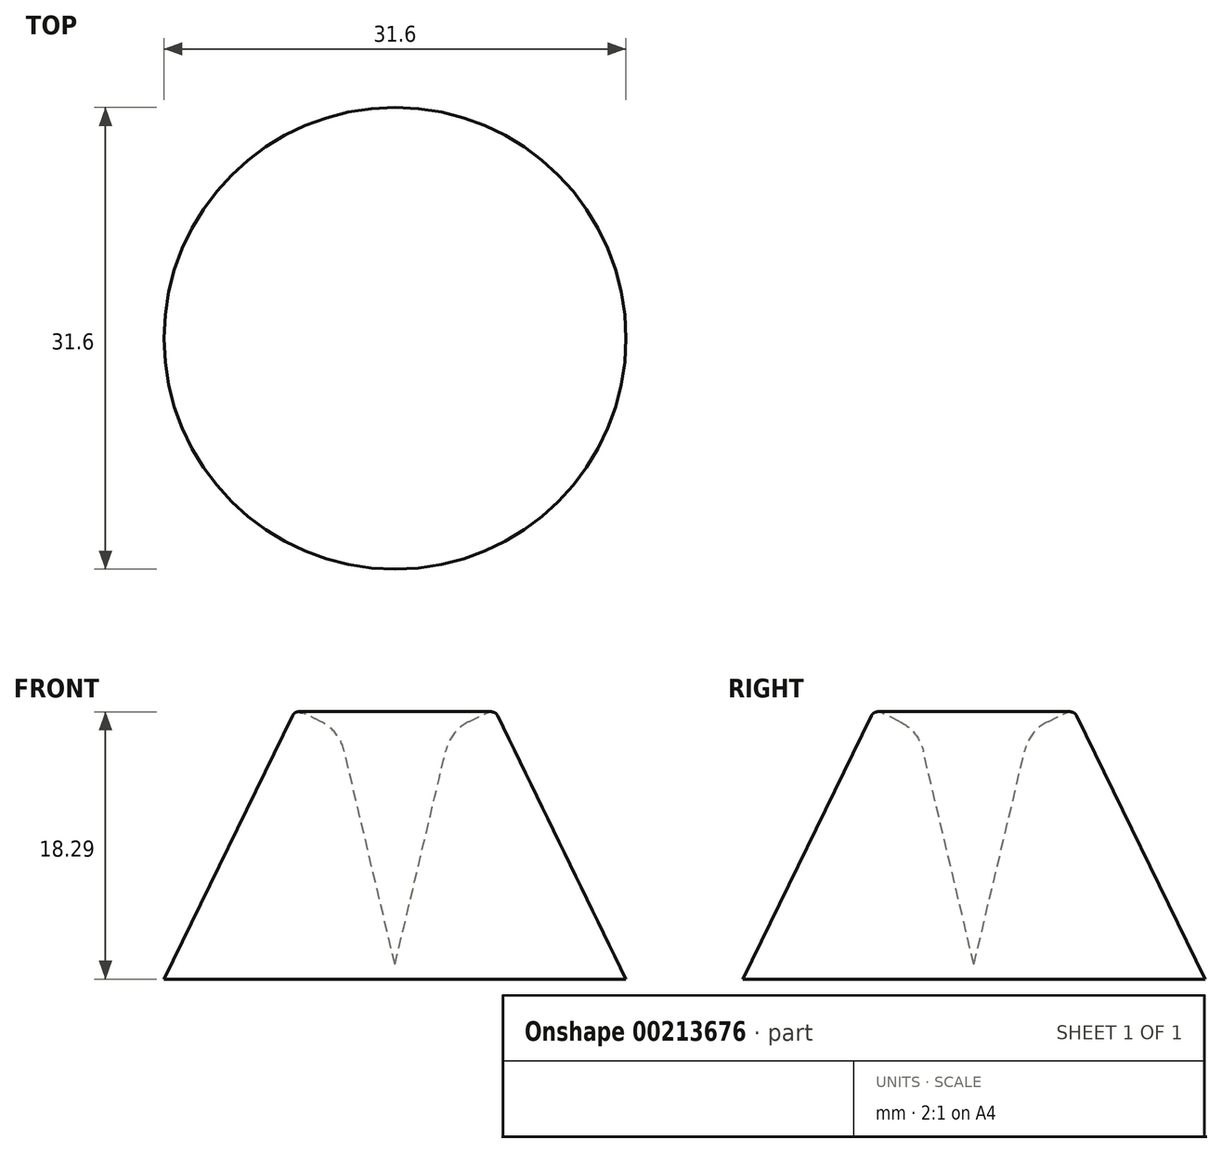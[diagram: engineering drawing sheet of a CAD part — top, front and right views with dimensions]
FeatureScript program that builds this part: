
annotation { "Feature Type Name" : "Feature", "Feature Type Description" : "" }
export const myFeature = defineFeature(function(context is Context, id is Id, definition is map)
    precondition{}
    {
        {
            var Q0;
            Q0=qCreatedBy(makeId("Front.planeOp"),FACE);
            var sketch = newSketch(context, id + "F0", { "sketchPlane" : qUnion([Q0])});
            skLineSegment(sketch, "E0", {"start": v(0, 0) * mm, "end": v(15.8, 0) * mm});
            skLineSegment(sketch, "E1", {"start": v(15.8, 0) * mm, "end": v(6.8, 18.46) * mm});
            skLineSegment(sketch, "E2", {"start": v(6.8, 18.46) * mm, "end": v(3.8, 17) * mm});
            skLineSegment(sketch, "E3", {"start": v(3.8, 17) * mm, "end": v(0, 1) * mm});
            skLineSegment(sketch, "E4", {"start": v(0, 1) * mm, "end": v(0, 0) * mm});
            skSolve(sketch);
        }
        {
            var Q0;
            Q0=makeQuery(id+"F0.imprint","IMPRINT",FACE,{"disambiguationData":[TD([[makeQuery(id+"F0.imprint","IMPRINT",EDGE,{"derivedFrom":sQuery(id+"F0.wireOp",EDGE,"E0")}),1.0]])]});
            var Q1;
            Q1=sQuery(id+"F0.wireOp",EDGE,"E4");
            revolve(context, id + "F1", {"entities" : qUnion([Q0]), "axis" : qUnion([Q1]), "revolveType" : RevolveType.FULL});
        }
        {
            var Q0;
            Q0=makeQuery(id+"F1.opRevolve","SWEPT_FACE",FACE,{"disambiguationData":[OSD([sQuery(id+"F0.wireOp",EDGE,"E3")])]});
            fillet(context, id + "F2", {"entities" : qUnion([Q0]), "radius" : 3 * mm, "tangentPropagation" : true, "allowEdgeOverflow" : false});
        }
        {
            var Q0;
            Q0=makeQuery(id+"F1.opRevolve","SWEPT_EDGE",EDGE,{"disambiguationData":[OSD([sQuery(id+"F0.wireOp",EDGE,"E1"),sQuery(id+"F0.wireOp",EDGE,"E2")])]});
            fillet(context, id + "F3", {"entities" : qUnion([Q0]), "radius" : 0.5 * mm, "tangentPropagation" : true, "allowEdgeOverflow" : false});
        }
    });
